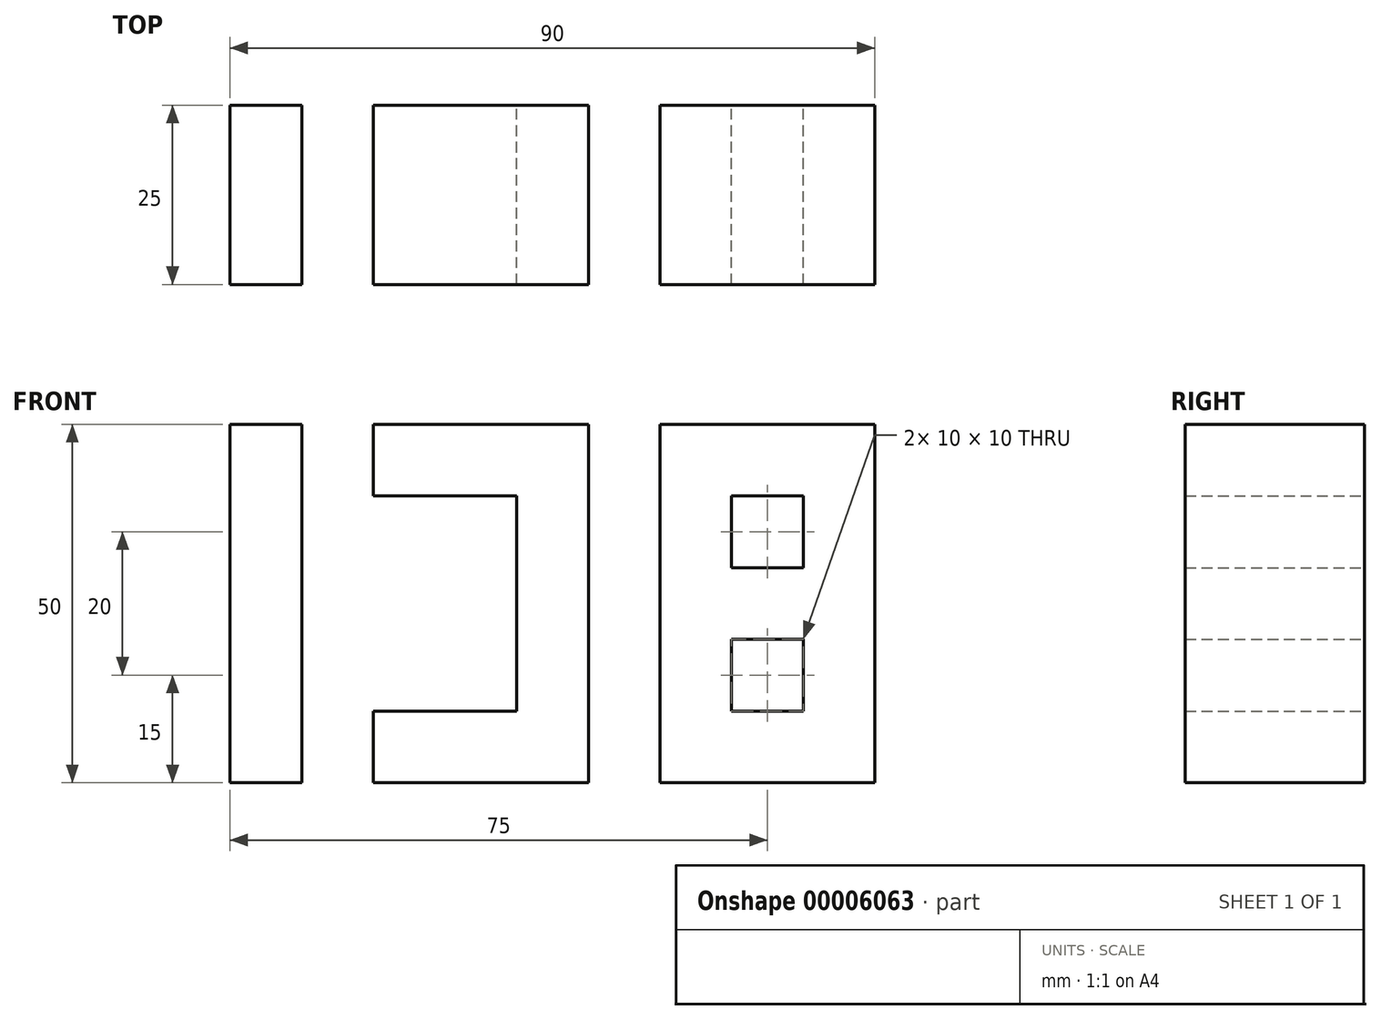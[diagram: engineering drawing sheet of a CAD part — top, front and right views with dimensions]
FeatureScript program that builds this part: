
annotation { "Feature Type Name" : "Feature", "Feature Type Description" : "" }
export const myFeature = defineFeature(function(context is Context, id is Id, definition is map)
    precondition{}
    {
        {
            var Q0;
            Q0=qCreatedBy(makeId("Front.planeOp"),FACE);
            var sketch = newSketch(context, id + "F0", { "sketchPlane" : qUnion([Q0])});
            skLineSegment(sketch, "E0.bottom", {"start": v(0, 0) * mm, "end": v(20, 0) * mm});
            skLineSegment(sketch, "E0.top", {"start": v(0, 50) * mm, "end": v(20, 50) * mm});
            skLineSegment(sketch, "E0.left", {"start": v(0, 0) * mm, "end": v(0, 50) * mm});
            skLineSegment(sketch, "E0.right", {"start": v(20, 0) * mm, "end": v(20, 50) * mm});
            skLineSegment(sketch, "E1.bottom", {"start": v(20, 50) * mm, "end": v(30, 50) * mm});
            skLineSegment(sketch, "E1.top", {"start": v(20, 0) * mm, "end": v(30, 0) * mm});
            skLineSegment(sketch, "E1.left", {"start": v(20, 50) * mm, "end": v(20, 0) * mm});
            skLineSegment(sketch, "E1.right", {"start": v(30, 50) * mm, "end": v(30, 0) * mm});
            skLineSegment(sketch, "E2.bottom", {"start": v(30, 50) * mm, "end": v(40, 50) * mm});
            skLineSegment(sketch, "E2.top", {"start": v(30, 0) * mm, "end": v(40, 0) * mm});
            skLineSegment(sketch, "E2.right", {"start": v(40, 50) * mm, "end": v(40, 0) * mm});
            skLineSegment(sketch, "E3.bottom", {"start": v(40, 50) * mm, "end": v(60, 50) * mm});
            skLineSegment(sketch, "E3.top", {"start": v(40, 40) * mm, "end": v(60, 40) * mm});
            skLineSegment(sketch, "E3.left", {"start": v(40, 50) * mm, "end": v(40, 40) * mm});
            skLineSegment(sketch, "E3.right", {"start": v(60, 50) * mm, "end": v(60, 40) * mm});
            skLineSegment(sketch, "E4.top", {"start": v(40, 30) * mm, "end": v(60, 30) * mm});
            skLineSegment(sketch, "E4.left", {"start": v(40, 40) * mm, "end": v(40, 30) * mm});
            skLineSegment(sketch, "E4.right", {"start": v(60, 40) * mm, "end": v(60, 30) * mm});
            skLineSegment(sketch, "E5.bottom", {"start": v(60, 30) * mm, "end": v(40, 30) * mm});
            skLineSegment(sketch, "E5.top", {"start": v(60, 20) * mm, "end": v(40, 20) * mm});
            skLineSegment(sketch, "E5.left", {"start": v(60, 30) * mm, "end": v(60, 20) * mm});
            skLineSegment(sketch, "E5.right", {"start": v(40, 30) * mm, "end": v(40, 20) * mm});
            skLineSegment(sketch, "E6.top", {"start": v(60, 10) * mm, "end": v(40, 10) * mm});
            skLineSegment(sketch, "E6.left", {"start": v(60, 20) * mm, "end": v(60, 10) * mm});
            skLineSegment(sketch, "E6.right", {"start": v(40, 20) * mm, "end": v(40, 10) * mm});
            skLineSegment(sketch, "E7.top", {"start": v(60, 0) * mm, "end": v(40, 0) * mm});
            skLineSegment(sketch, "E7.left", {"start": v(60, 10) * mm, "end": v(60, 0) * mm});
            skLineSegment(sketch, "E7.right", {"start": v(40, 10) * mm, "end": v(40, 0) * mm});
            skLineSegment(sketch, "E8.bottom", {"start": v(60, 50) * mm, "end": v(70, 50) * mm});
            skLineSegment(sketch, "E8.top", {"start": v(60, 0) * mm, "end": v(70, 0) * mm});
            skLineSegment(sketch, "E8.left", {"start": v(60, 50) * mm, "end": v(60, 0) * mm});
            skLineSegment(sketch, "E8.right", {"start": v(70, 50) * mm, "end": v(70, 0) * mm});
            skLineSegment(sketch, "E9.bottom", {"start": v(70, 50) * mm, "end": v(80, 50) * mm});
            skLineSegment(sketch, "E9.top", {"start": v(70, 0) * mm, "end": v(80, 0) * mm});
            skLineSegment(sketch, "E9.right", {"start": v(80, 50) * mm, "end": v(80, 0) * mm});
            skLineSegment(sketch, "E10.bottom", {"start": v(80, 50) * mm, "end": v(90, 50) * mm});
            skLineSegment(sketch, "E10.top", {"start": v(80, 0) * mm, "end": v(90, 0) * mm});
            skLineSegment(sketch, "E10.right", {"start": v(90, 50) * mm, "end": v(90, 0) * mm});
            skLineSegment(sketch, "E11.bottom", {"start": v(90, 50) * mm, "end": v(100, 50) * mm});
            skLineSegment(sketch, "E11.top", {"start": v(90, 40) * mm, "end": v(100, 40) * mm});
            skLineSegment(sketch, "E11.left", {"start": v(90, 50) * mm, "end": v(90, 40) * mm});
            skLineSegment(sketch, "E11.right", {"start": v(100, 50) * mm, "end": v(100, 40) * mm});
            skLineSegment(sketch, "E12.top", {"start": v(90, 30) * mm, "end": v(100, 30) * mm});
            skLineSegment(sketch, "E12.left", {"start": v(90, 40) * mm, "end": v(90, 30) * mm});
            skLineSegment(sketch, "E12.right", {"start": v(100, 40) * mm, "end": v(100, 30) * mm});
            skLineSegment(sketch, "E13.top", {"start": v(90, 20) * mm, "end": v(100, 20) * mm});
            skLineSegment(sketch, "E13.left", {"start": v(90, 30) * mm, "end": v(90, 20) * mm});
            skLineSegment(sketch, "E13.right", {"start": v(100, 30) * mm, "end": v(100, 20) * mm});
            skLineSegment(sketch, "E14.top", {"start": v(90, 10) * mm, "end": v(100, 10) * mm});
            skLineSegment(sketch, "E14.left", {"start": v(90, 20) * mm, "end": v(90, 10) * mm});
            skLineSegment(sketch, "E14.right", {"start": v(100, 20) * mm, "end": v(100, 10) * mm});
            skLineSegment(sketch, "E15.top", {"start": v(90, 0) * mm, "end": v(100, 0) * mm});
            skLineSegment(sketch, "E15.left", {"start": v(90, 10) * mm, "end": v(90, 0) * mm});
            skLineSegment(sketch, "E15.right", {"start": v(100, 10) * mm, "end": v(100, 0) * mm});
            skLineSegment(sketch, "E16.bottom", {"start": v(100, 50) * mm, "end": v(110, 50) * mm});
            skLineSegment(sketch, "E16.top", {"start": v(100, 0) * mm, "end": v(110, 0) * mm});
            skLineSegment(sketch, "E16.left", {"start": v(100, 50) * mm, "end": v(100, 0) * mm});
            skLineSegment(sketch, "E16.right", {"start": v(110, 50) * mm, "end": v(110, 0) * mm});
            skLineSegment(sketch, "E17.bottom", {"start": v(0, 50) * mm, "end": v(10, 50) * mm});
            skLineSegment(sketch, "E17.top", {"start": v(0, 0) * mm, "end": v(10, 0) * mm});
            skLineSegment(sketch, "E17.left", {"start": v(0, 50) * mm, "end": v(0, 0) * mm});
            skLineSegment(sketch, "E17.right", {"start": v(10, 50) * mm, "end": v(10, 0) * mm});
            skSolve(sketch);
        }
        {
            var Q0;
            Q0=makeQuery(id+"F0.imprint","IMPRINT",FACE,{"disambiguationData":[TD([[makeQuery(id+"F0.imprint","IMPRINT",EDGE,{"derivedFrom":sQuery(id+"F0.wireOp",EDGE,"E17.bottom")}),-1.0]])]});
            var Q1;
            Q1=makeQuery(id+"F0.imprint","IMPRINT",FACE,{"disambiguationData":[TD([[makeQuery(id+"F0.imprint","IMPRINT",EDGE,{"derivedFrom":sQuery(id+"F0.wireOp",EDGE,"E1.bottom")}),-1.0]])]});
            var Q2;
            {var subQ2=sQuery(id+"F0.wireOp",EDGE,"E3.bottom");Q2=makeQuery(id+"F0.imprint","IMPRINT",FACE,{"disambiguationData":[TD([[makeQuery(id+"F0.imprint","IMPRINT",EDGE,{"derivedFrom":subQ2}),-1.0]])]});}
            var Q3;
            {var subQ2=sQuery(id+"F0.wireOp",EDGE,"E5.bottom");Q3=makeQuery(id+"F0.imprint","IMPRINT",FACE,{"disambiguationData":[TD([[makeQuery(id+"F0.imprint","IMPRINT",EDGE,{"derivedFrom":subQ2}),1.0]])]});}
            var Q4;
            {var subQ2=sQuery(id+"F0.wireOp",EDGE,"E6.top");Q4=makeQuery(id+"F0.imprint","IMPRINT",FACE,{"disambiguationData":[TD([[makeQuery(id+"F0.imprint","IMPRINT",EDGE,{"derivedFrom":subQ2}),1.0]])]});}
            var Q5;
            {var subQ6=sQuery(id+"F0.wireOp",EDGE,"E8.bottom");Q5=makeQuery(id+"F0.imprint","IMPRINT",FACE,{"disambiguationData":[TD([[makeQuery(id+"F0.imprint","IMPRINT",EDGE,{"derivedFrom":subQ6}),-1.0]])]});}
            var Q6;
            Q6=makeQuery(id+"F0.imprint","IMPRINT",FACE,{"disambiguationData":[TD([[makeQuery(id+"F0.imprint","IMPRINT",EDGE,{"derivedFrom":sQuery(id+"F0.wireOp",EDGE,"E10.bottom")}),-1.0]])]});
            var Q7;
            {var subQ2=sQuery(id+"F0.wireOp",EDGE,"E11.bottom");Q7=makeQuery(id+"F0.imprint","IMPRINT",FACE,{"disambiguationData":[TD([[makeQuery(id+"F0.imprint","IMPRINT",EDGE,{"derivedFrom":subQ2}),-1.0]])]});}
            var Q8;
            {var subQ6=sQuery(id+"F0.wireOp",EDGE,"E16.bottom");Q8=makeQuery(id+"F0.imprint","IMPRINT",FACE,{"disambiguationData":[TD([[makeQuery(id+"F0.imprint","IMPRINT",EDGE,{"derivedFrom":subQ6}),-1.0]])]});}
            var Q9;
            {var subQ2=sQuery(id+"F0.wireOp",EDGE,"E12.top");Q9=makeQuery(id+"F0.imprint","IMPRINT",FACE,{"disambiguationData":[TD([[makeQuery(id+"F0.imprint","IMPRINT",EDGE,{"derivedFrom":subQ2}),-1.0]])]});}
            var Q10;
            {var subQ2=sQuery(id+"F0.wireOp",EDGE,"E14.top");Q10=makeQuery(id+"F0.imprint","IMPRINT",FACE,{"disambiguationData":[TD([[makeQuery(id+"F0.imprint","IMPRINT",EDGE,{"derivedFrom":subQ2}),-1.0]])]});}
            extrude(context, id + "F1", {"entities" : qUnion([Q0, Q1, Q2, Q3, Q4, Q5, Q6, Q7, Q8, Q9, Q10]), "depth" : 25 * mm});
        }
    });
